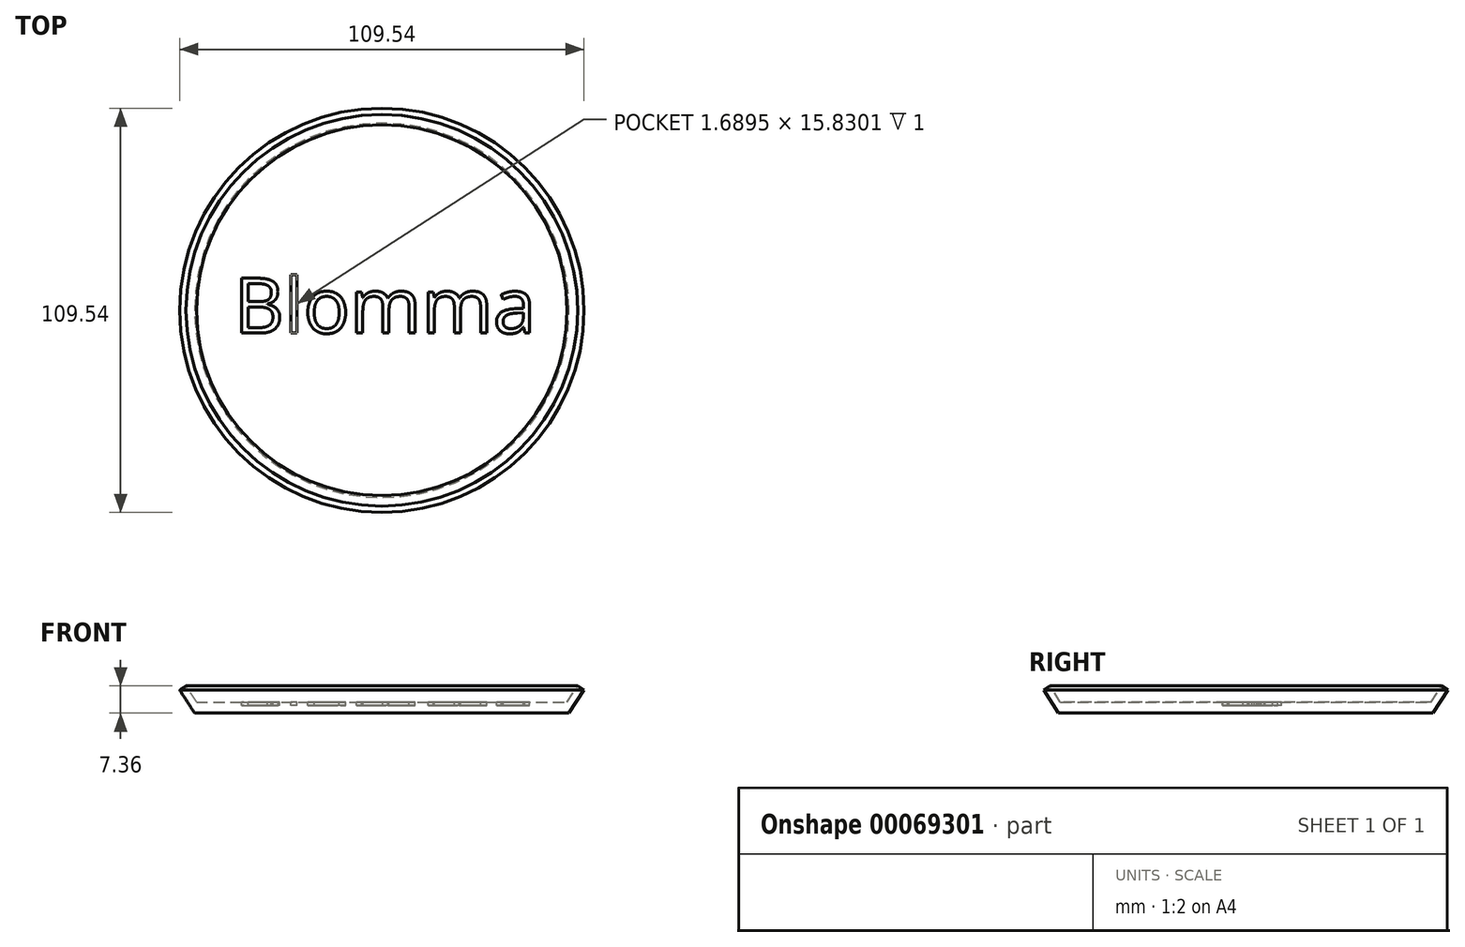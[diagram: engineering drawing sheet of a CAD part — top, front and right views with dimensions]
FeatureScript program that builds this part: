
annotation { "Feature Type Name" : "Feature", "Feature Type Description" : "" }
export const myFeature = defineFeature(function(context is Context, id is Id, definition is map)
    precondition{}
    {
        {
            var Q0;
            Q0=qCreatedBy(makeId("Front.planeOp"),FACE);
            var sketch = newSketch(context, id + "F0", { "sketchPlane" : qUnion([Q0])});
            skLineSegment(sketch, "E0", {"start": v(50.72, 0) * mm, "end": v(54.77, 6.24) * mm});
            skLineSegment(sketch, "E1", {"start": v(54.77, 6.24) * mm, "end": v(53.04, 7.36) * mm});
            skLineSegment(sketch, "E2", {"start": v(53.04, 7.36) * mm, "end": v(50.22, 3) * mm});
            skLineSegment(sketch, "E3", {"start": v(50.22, 3) * mm, "end": v(0, 3) * mm});
            skLineSegment(sketch, "E4", {"start": v(0, 3) * mm, "end": v(0, 0) * mm});
            skLineSegment(sketch, "E5", {"start": v(0, 0) * mm, "end": v(50.72, 0) * mm});
            skLineSegment(sketch, "E6", {"start": v(0, 3) * mm, "end": v(0, 7.47) * mm, "construction": true});
            skSolve(sketch);
        }
        {
            var Q0;
            Q0=makeQuery(id+"F0.imprint","IMPRINT",FACE,{"disambiguationData":[TD([[makeQuery(id+"F0.imprint","IMPRINT",EDGE,{"derivedFrom":sQuery(id+"F0.wireOp",EDGE,"E0")}),1.0]])]});
            var Q1;
            Q1=sQuery(id+"F0.wireOp",EDGE,"E6");
            revolve(context, id + "F1", {"entities" : qUnion([Q0]), "axis" : qUnion([Q1]), "revolveType" : RevolveType.FULL});
        }
        {
            var Q0;
            Q0=makeQuery(id+"F1.opRevolve","SWEPT_FACE",FACE,{"disambiguationData":[OSD([sQuery(id+"F0.wireOp",EDGE,"E3")])]});
            var sketch = newSketch(context, id + "F2", { "sketchPlane" : qUnion([Q0])});
            skText(sketch, "E7", { "text": "Blomma", "fontName": "OpenSans-Regular.ttf"});
            const initialGuessF2  = {"E7": [-0.04, -0.00616, 1, 0, 0.015]};
            skSetInitialGuess(sketch, initialGuessF2);
            skSolve(sketch);
        }
        {
            var Q0;
            Q0 = qSketchRegion(id + "F2", true);
            extrude(context, id + "F3", {"entities" : qUnion([Q0]), "operationType" : NewBodyOperationType.REMOVE, "oppositeDirection" : true, "depth" : 1 * mm});
        }
    });
